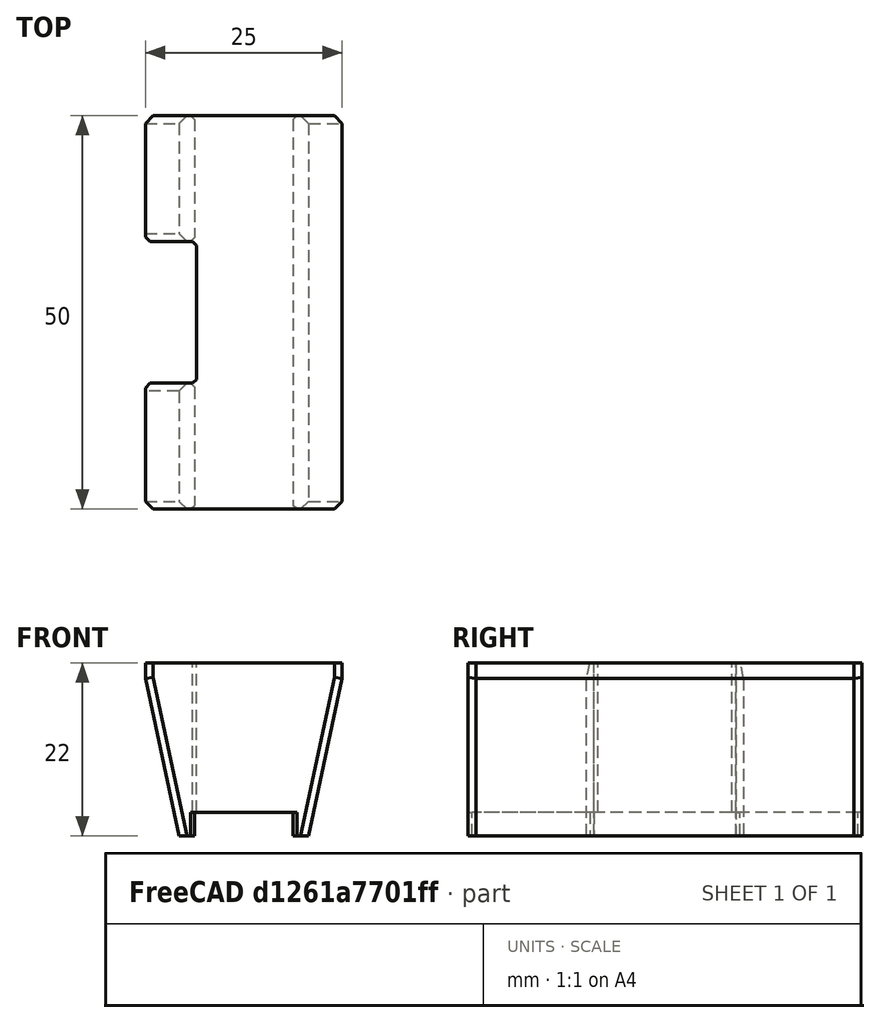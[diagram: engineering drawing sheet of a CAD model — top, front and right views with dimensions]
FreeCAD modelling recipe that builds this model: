
FCSTD DOCUMENT  (FreeCAD 0.19R)
Label: 19mmCabinetSpace
License: All rights reserved
LicenseURL: http://en.wikipedia.org/wiki/All_rights_reserved
objects: PartDesign::Chamfer×4, Sketcher::SketchObject×2, PartDesign::Pad×1, PartDesign::Pocket×1, PartDesign::Body×1, Mesh::Feature×1
note: 15 computed .brp shape members not serialized (recipe doc carries the construction recipe); baked Part::Feature solids carry a one-line shape summary decoded from their .brp

FEATURE [Sketcher::SketchObject] Sketch
  FullyConstrained = true
  MapMode = 5
  Placement = pos=(0,0,0) rot=(1,0,0;1.5708rad)
  Support = -> [XZ_Plane]
  sketch-geometry (10):
    g0: LineSegment StartX=-12.5 StartY=0 StartZ=0 EndX=-12.5 EndY=-2 EndZ=0
    g1: LineSegment StartX=-12.5 StartY=-2 StartZ=0 EndX=-8.25 EndY=-22 EndZ=0
    g2: LineSegment StartX=-8.25 StartY=-22 StartZ=0 EndX=-6.25 EndY=-22 EndZ=0
    g3: LineSegment StartX=-6.25 StartY=-22 StartZ=0 EndX=-6.25 EndY=-19 EndZ=0
    g4: LineSegment StartX=-6.25 StartY=-19 StartZ=0 EndX=6.25 EndY=-19 EndZ=0
    g5: LineSegment StartX=6.25 StartY=-19 StartZ=0 EndX=6.25 EndY=-22 EndZ=0
    g6: LineSegment StartX=6.25 StartY=-22 StartZ=0 EndX=8.25 EndY=-22 EndZ=0
    g7: LineSegment StartX=8.25 StartY=-22 StartZ=0 EndX=12.5 EndY=-2 EndZ=0
    g8: LineSegment StartX=12.5 StartY=-2 StartZ=0 EndX=12.5 EndY=0 EndZ=0
    g9: LineSegment StartX=12.5 StartY=0 StartZ=0 EndX=-12.5 EndY=0 EndZ=0
  constraints (25):
    c: PointOnObject(g0,g-1)
    c: Vertical(g0)
    c: Coincident(g0,g1)
    c: Coincident(g1,g2)
    c: Horizontal(g2)
    c: Coincident(g2,g3)
    c: Vertical(g3)
    c: Coincident(g3,g4)
    c: Coincident(g4,g5)
    c: Coincident(g5,g6)
    c: Coincident(g6,g7)
    c: Coincident(g7,g8)
    c: Coincident(g8,g9)
    c: Coincident(g9,g0)
    c: Symmetric(g4,g3,g-2)
    c: Symmetric(g6,g1,g-2)
    c: Symmetric(g5,g2,g-2)
    c: Symmetric(g0,g7,g-2)
    c: Symmetric(g8,g0,g-2)
    c: Distance(g8) = 2
    c: Distance(g6) = 2
    c: Distance(g4) = 12.5
    c: Distance(g9) = 25
    c: Distance(g3) = 3
    c: DistanceY(g3) = -19
FEATURE [PartDesign::Pad] Pad
  Direction = (1,1,1)
  Length = 50
  Length2 = 100
  Placement = pos=(0,0,0) rot=(1,0,0;1.5708rad)
  Profile = -> Sketch
  Type = 0
FEATURE [Sketcher::SketchObject] Sketch001
  FullyConstrained = false
  MapMode = 5
  Placement = pos=(0,-1.47e-14,-22) rot=(1,0,0;3.14159rad)
  Support = -> [Pad]
  sketch-geometry (5):
    g0: LineSegment StartX=-31.4883 StartY=34 StartZ=0 EndX=-6 EndY=34 EndZ=0
    g1: LineSegment StartX=-6 StartY=34 StartZ=0 EndX=-6 EndY=16 EndZ=0
    g2: LineSegment StartX=-6 StartY=16 StartZ=0 EndX=-31.4883 EndY=16 EndZ=0
    g3: LineSegment StartX=-31.4883 StartY=16 StartZ=0 EndX=-31.4883 EndY=34 EndZ=0
    g4: LineSegment StartX=-43.1504 StartY=25 StartZ=0 EndX=42.9752 EndY=25 EndZ=0
  constraints (12):
    c: Coincident(g0,g1)
    c: Coincident(g1,g2)
    c: Coincident(g2,g3)
    c: Coincident(g3,g0)
    c: Horizontal(g0)
    c: Horizontal(g2)
    c: Vertical(g1)
    c: Vertical(g3)
    c: Distance(g1) = 18
    c: Symmetric(g2,g0,g4)
    c: DistanceY(g4) = 25
    c: DistanceX(g1) = -6
FEATURE [PartDesign::Pocket] Pocket
  BaseFeature = -> Pad
  Length = 5
  Length2 = 100
  Placement = pos=(0,0,0) rot=(1,0,0;1.5708rad)
  Profile = -> Sketch001
  Type = 1
FEATURE [PartDesign::Chamfer] Chamfer
  Angle = 45
  Base = -> Pocket [Edge11,Edge38,Edge12,Edge39,Edge46,Edge47,Edge1,Edge5]
  BaseFeature = -> Pocket
  ChamferType = 0
  FlipDirection = false
  Placement = pos=(0,0,0) rot=(1,0,0;1.5708rad)
  Size = 1
  Size2 = 1
  SupportTransform = false
FEATURE [PartDesign::Chamfer] Chamfer001
  Angle = 45
  Base = -> Chamfer [Edge7,Edge60]
  BaseFeature = -> Chamfer
  ChamferType = 0
  FlipDirection = false
  Placement = pos=(0,0,0) rot=(1,0,0;1.5708rad)
  Size = 1
  Size2 = 1
  SupportTransform = false
FEATURE [PartDesign::Chamfer] Chamfer002
  Angle = 45
  Base = -> Chamfer001 [Edge35,Edge33,Edge30,Edge45,Edge58,Edge61]
  BaseFeature = -> Chamfer001
  ChamferType = 0
  FlipDirection = false
  Placement = pos=(0,0,0) rot=(1,0,0;1.5708rad)
  Size = 0.5
  Size2 = 1
  SupportTransform = false
FEATURE [PartDesign::Chamfer] Chamfer003
  Angle = 45
  Base = -> Chamfer002 [Edge60,Edge14]
  BaseFeature = -> Chamfer002
  ChamferType = 0
  FlipDirection = false
  Placement = pos=(0,0,0) rot=(1,0,0;1.5708rad)
  Size = 0.5
  Size2 = 1
  SupportTransform = false
FEATURE [PartDesign::Body] Body
  Group = -> [Sketch,Pad,Sketch001,Pocket,Chamfer,Chamfer001,Chamfer002,Chamfer003]
  Origin = -> Origin
  Tip = -> Chamfer003
FEATURE [Mesh::Feature] Mesh  label="Chamfer003 (Meshed)"
